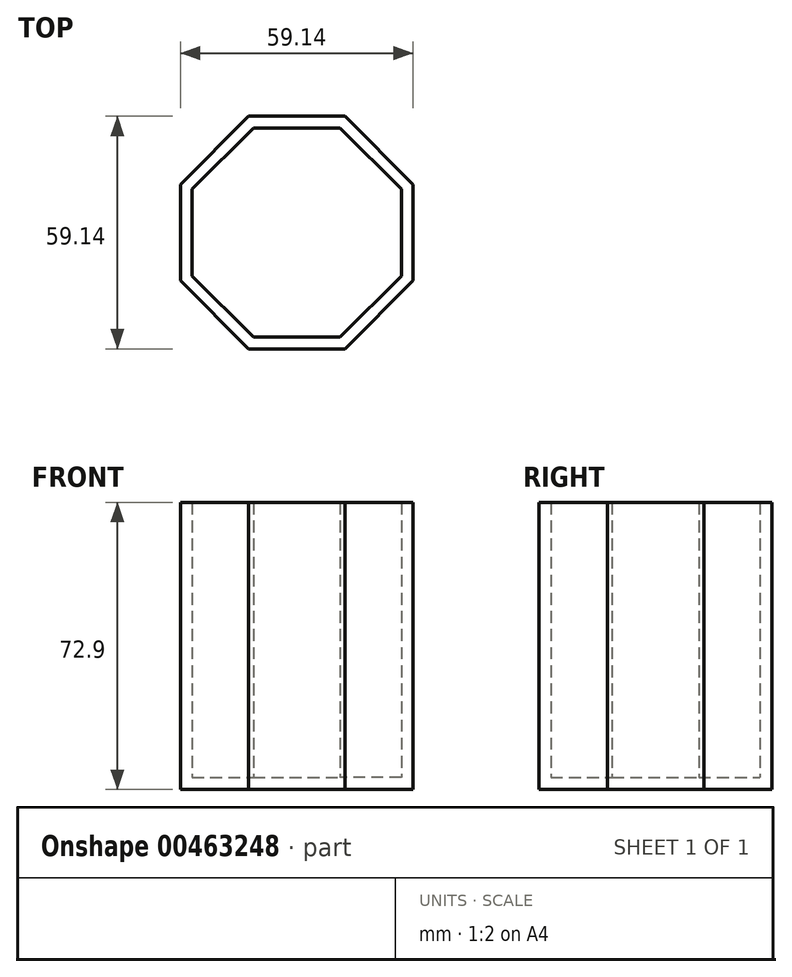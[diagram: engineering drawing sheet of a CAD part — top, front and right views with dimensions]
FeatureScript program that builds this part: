
annotation { "Feature Type Name" : "Feature", "Feature Type Description" : "" }
export const myFeature = defineFeature(function(context is Context, id is Id, definition is map)
    precondition{}
    {
        {
            var Q0;
            Q0=qCreatedBy(makeId("Top.planeOp"),FACE);
            var sketch = newSketch(context, id + "F0", { "sketchPlane" : qUnion([Q0])});
            skCircle(sketch, "E0.cCircle", {"center": v(0, 0) * mm, "radius": 29.57 * mm, "construction": true});
            skLineSegment(sketch, "E0.0", {"start": v(-12.25, 29.57) * mm, "end": v(12.25, 29.57) * mm});
            skLineSegment(sketch, "E0.1", {"start": v(12.25, 29.57) * mm, "end": v(29.57, 12.25) * mm});
            skLineSegment(sketch, "E0.2", {"start": v(29.57, 12.25) * mm, "end": v(29.57, -12.25) * mm});
            skLineSegment(sketch, "E0.3", {"start": v(29.57, -12.25) * mm, "end": v(12.25, -29.57) * mm});
            skLineSegment(sketch, "E0.4", {"start": v(12.25, -29.57) * mm, "end": v(-12.25, -29.57) * mm});
            skLineSegment(sketch, "E0.5", {"start": v(-12.25, -29.57) * mm, "end": v(-29.57, -12.25) * mm});
            skLineSegment(sketch, "E0.6", {"start": v(-29.57, -12.25) * mm, "end": v(-29.57, 12.25) * mm});
            skLineSegment(sketch, "E0.7", {"start": v(-29.57, 12.25) * mm, "end": v(-12.25, 29.57) * mm});
            skPoint(sketch, "E0.0.midPoint", {"position": v(0, 29.57) * mm});
            skSolve(sketch);
        }
        {
            var Q0;
            Q0=makeQuery(id+"F0.imprint","IMPRINT",FACE,{"disambiguationData":[TD([[makeQuery(id+"F0.imprint","IMPRINT",EDGE,{"derivedFrom":sQuery(id+"F0.wireOp",EDGE,"E0.0")}),-1.0]])]});
            extrude(context, id + "F1", {"entities" : qUnion([Q0]), "depth" : 72.9 * mm});
        }
        {
            var Q0;
            Q0=makeQuery(id+"F1.opExtrude","CAP_FACE",FACE,{"disambiguationData":[OSD([sQuery(id+"F0.wireOp",EDGE,"E0.0"),sQuery(id+"F0.wireOp",EDGE,"E0.1"),sQuery(id+"F0.wireOp",EDGE,"E0.2"),sQuery(id+"F0.wireOp",EDGE,"E0.3"),sQuery(id+"F0.wireOp",EDGE,"E0.4"),sQuery(id+"F0.wireOp",EDGE,"E0.5"),sQuery(id+"F0.wireOp",EDGE,"E0.6"),sQuery(id+"F0.wireOp",EDGE,"E0.7")])],"isStart":false});
            shell(context, id + "F2", {"entities" : qUnion([Q0]), "thickness" : 3 * mm});
        }
    });
